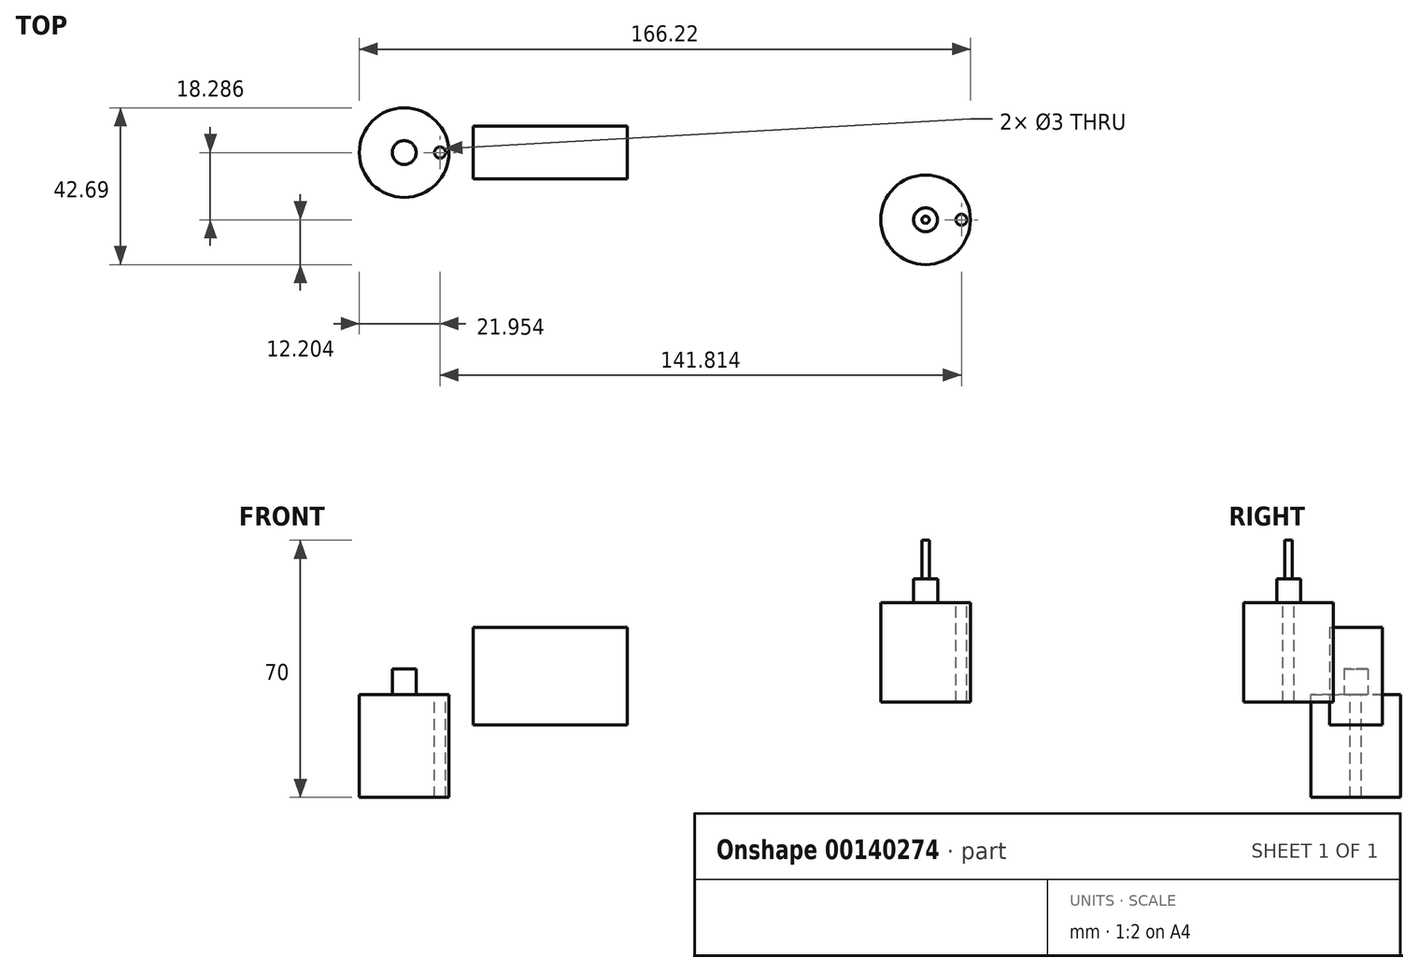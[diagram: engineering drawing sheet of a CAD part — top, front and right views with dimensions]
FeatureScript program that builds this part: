
annotation { "Feature Type Name" : "Feature", "Feature Type Description" : "" }
export const myFeature = defineFeature(function(context is Context, id is Id, definition is map)
    precondition{}
    {
        {
            var Q0;
            Q0=qCreatedBy(makeId("Front.planeOp"),FACE);
            var sketch = newSketch(context, id + "F0", { "sketchPlane" : qUnion([Q0])});
            skLineSegment(sketch, "E0.bottom", {"start": v(21, 13.25) * mm, "end": v(-21, 13.25) * mm});
            skLineSegment(sketch, "E0.top", {"start": v(21, -13.25) * mm, "end": v(-21, -13.25) * mm});
            skLineSegment(sketch, "E0.left", {"start": v(21, 13.25) * mm, "end": v(21, -13.25) * mm});
            skLineSegment(sketch, "E0.right", {"start": v(-21, 13.25) * mm, "end": v(-21, -13.25) * mm});
            skPoint(sketch, "E0.middle", {"position": v(0, 0) * mm});
            skSolve(sketch);
        }
        {
            var Q0;
            Q0 = qSketchRegion(id + "F0", true);
            extrude(context, id + "F1", {"entities" : qUnion([Q0]), "endBound" : BoundingType.SYMMETRIC, "depth" : 14.3 * mm});
        }
        {
            var Q0;
            Q0=makeQuery(id+"F1.opExtrude","CAP_FACE",FACE,{"disambiguationData":[OSD([sQuery(id+"F0.wireOp",EDGE,"E0.bottom"),sQuery(id+"F0.wireOp",EDGE,"E0.top"),sQuery(id+"F0.wireOp",EDGE,"E0.left"),sQuery(id+"F0.wireOp",EDGE,"E0.right")])],"isStart":false});
            cPlane(context, id + "F2", {"entities" : qUnion([Q0]), "cplaneType" : CPlaneType.OFFSET, "offset" : 0 * mm, "width" : 150 * mm, "height" : 150 * mm});
        }
        {
            var Q0;
            Q0=qCreatedBy(makeId("Top.planeOp"),FACE);
            var sketch = newSketch(context, id + "F3", { "sketchPlane" : qUnion([Q0])});
            skLineSegment(sketch, "E1", {"start": v(-39.74, 30.29) * mm, "end": v(-39.74, -34.47) * mm, "construction": true});
            skCircle(sketch, "E2", {"center": v(-39.74, 0) * mm, "radius": 12.2 * mm});
            skLineSegment(sketch, "E3.0", {"start": v(-49.49, 30.29) * mm, "end": v(-49.49, -34.47) * mm, "construction": true});
            skCircle(sketch, "E4", {"center": v(-49.49, 0) * mm, "radius": 1.5 * mm});
            skCircle(sketch, "E5.MirrorC", {"center": v(-29.99, 0) * mm, "radius": 1.5 * mm});
            skLineSegment(sketch, "E6.MirrorCS", {"start": v(-29.99, 30.29) * mm, "end": v(-29.99, -34.47) * mm, "construction": true});
            skCircle(sketch, "E7", {"center": v(-39.74, 0) * mm, "radius": 3.25 * mm});
            skCircle(sketch, "E8", {"center": v(-39.74, 0) * mm, "radius": 1 * mm});
            skSolve(sketch);
        }
        {
            var Q0;
            Q0=makeQuery(id+"F3.imprint","IMPRINT",FACE,{"disambiguationData":[TD([[makeQuery(id+"F3.imprint","IMPRINT",EDGE,{"derivedFrom":sQuery(id+"F3.wireOp",EDGE,"E4")}),1.0]])]});
            var Q1;
            Q1=makeQuery(id+"F3.imprint","IMPRINT",FACE,{"disambiguationData":[TD([[makeQuery(id+"F3.imprint","IMPRINT",EDGE,{"derivedFrom":sQuery(id+"F3.wireOp",EDGE,"E5.MirrorC")}),-1.0]])]});
            var Q2;
            Q2=makeQuery(id+"F3.imprint","IMPRINT",FACE,{"disambiguationData":[TD([[makeQuery(id+"F3.imprint","IMPRINT",EDGE,{"derivedFrom":sQuery(id+"F3.wireOp",EDGE,"E2")}),1.0]])]});
            var Q3;
            Q3=makeQuery(id+"F3.imprint","IMPRINT",FACE,{"disambiguationData":[TD([[makeQuery(id+"F3.imprint","IMPRINT",EDGE,{"derivedFrom":sQuery(id+"F3.wireOp",EDGE,"E7")}),1.0]])]});
            var Q4;
            Q4=makeQuery(id+"F3.imprint","IMPRINT",FACE,{"disambiguationData":[TD([[makeQuery(id+"F3.imprint","IMPRINT",EDGE,{"derivedFrom":sQuery(id+"F3.wireOp",EDGE,"E8")}),1.0]])]});
            extrude(context, id + "F4", {"entities" : qUnion([Q0, Q1, Q2, Q3, Q4]), "oppositeDirection" : true, "depth" : 33 * mm});
        }
        {
            var Q0;
            Q0=makeQuery(id+"F3.imprint","IMPRINT",FACE,{"disambiguationData":[TD([[makeQuery(id+"F3.imprint","IMPRINT",EDGE,{"derivedFrom":sQuery(id+"F3.wireOp",EDGE,"E8")}),1.0]])]});
            var Q1;
            Q1=makeQuery(id+"F3.imprint","IMPRINT",FACE,{"disambiguationData":[TD([[makeQuery(id+"F3.imprint","IMPRINT",EDGE,{"derivedFrom":sQuery(id+"F3.wireOp",EDGE,"E7")}),1.0]])]});
            extrude(context, id + "F5", {"entities" : qUnion([Q0, Q1]), "operationType" : NewBodyOperationType.ADD, "depth" : 2 * mm});
        }
        {
            var Q0;
            Q0=sQuery(id+"F3.wireOp",EDGE,"E8");
            extrude(context, id + "F6", {"bodyType" : ToolBodyType.SURFACE, "surfaceEntities" : qUnion([Q0]), "depth" : 12 * mm});
        }
        {
            var Q0;
            Q0=makeQuery(id+"F3.imprint","IMPRINT",FACE,{"disambiguationData":[TD([[makeQuery(id+"F3.imprint","IMPRINT",EDGE,{"derivedFrom":sQuery(id+"F3.wireOp",EDGE,"E4")}),1.0]])]});
            var Q1;
            Q1=makeQuery(id+"F3.imprint","IMPRINT",FACE,{"disambiguationData":[TD([[makeQuery(id+"F3.imprint","IMPRINT",EDGE,{"derivedFrom":sQuery(id+"F3.wireOp",EDGE,"E5.MirrorC")}),-1.0]])]});
            extrude(context, id + "F7", {"entities" : qUnion([Q0, Q1]), "operationType" : NewBodyOperationType.REMOVE, "oppositeDirection" : true, "depth" : 5 * mm});
        }
        {
            var Q0;
            Q0=qCreatedBy(makeId("Top.planeOp"),FACE);
            cPlane(context, id + "F8", {"entities" : qUnion([Q0]), "cplaneType" : CPlaneType.OFFSET, "offset" : 25 * mm, "width" : 150 * mm, "height" : 150 * mm});
        }
        {
            var Q0;
            Q0=qCreatedBy(id+"F8.planeOp",FACE);
            var sketch = newSketch(context, id + "F9", { "sketchPlane" : qUnion([Q0])});
            skLineSegment(sketch, "E9", {"start": v(102.08, 12) * mm, "end": v(102.08, -52.76) * mm, "construction": true});
            skCircle(sketch, "E10", {"center": v(102.08, -18.29) * mm, "radius": 12.2 * mm});
            skLineSegment(sketch, "E11.0", {"start": v(92.33, -3.52) * mm, "end": v(92.33, -33.05) * mm, "construction": true});
            skCircle(sketch, "E12", {"center": v(92.33, -18.29) * mm, "radius": 1.5 * mm});
            skCircle(sketch, "E13.MirrorC", {"center": v(111.83, -18.29) * mm, "radius": 1.5 * mm});
            skLineSegment(sketch, "E14.MirrorCS", {"start": v(111.83, -3.52) * mm, "end": v(111.83, -33.05) * mm, "construction": true});
            skCircle(sketch, "E15", {"center": v(102.08, -18.29) * mm, "radius": 3.25 * mm});
            skCircle(sketch, "E16", {"center": v(102.08, -18.29) * mm, "radius": 1 * mm});
            skLineSegment(sketch, "E17", {"start": v(148.87, -18.29) * mm, "end": v(55.3, -18.29) * mm});
            skSolve(sketch);
        }
        {
            var Q0;
            Q0=makeQuery(id+"F9.imprint","IMPRINT",FACE,{"disambiguationData":[TD([[makeQuery(id+"F9.imprint","IMPRINT",EDGE,{"derivedFrom":sQuery(id+"F9.wireOp",EDGE,"E10")}),1.0]])]});
            var Q1;
            Q1=makeQuery(id+"F9.imprint","IMPRINT",FACE,{"disambiguationData":[TD([[makeQuery(id+"F9.imprint","IMPRINT",EDGE,{"derivedFrom":sQuery(id+"F9.wireOp",EDGE,"E13.MirrorC")}),-1.0]])]});
            var Q2;
            Q2=makeQuery(id+"F9.imprint","IMPRINT",FACE,{"disambiguationData":[TD([[makeQuery(id+"F9.imprint","IMPRINT",EDGE,{"derivedFrom":sQuery(id+"F9.wireOp",EDGE,"E15")}),1.0]])]});
            var Q3;
            Q3=makeQuery(id+"F9.imprint","IMPRINT",FACE,{"disambiguationData":[TD([[makeQuery(id+"F9.imprint","IMPRINT",EDGE,{"derivedFrom":sQuery(id+"F9.wireOp",EDGE,"E16")}),1.0]])]});
            var Q4;
            Q4=makeQuery(id+"F9.imprint","IMPRINT",FACE,{"disambiguationData":[TD([[makeQuery(id+"F9.imprint","IMPRINT",EDGE,{"derivedFrom":sQuery(id+"F9.wireOp",EDGE,"E12")}),1.0]])]});
            extrude(context, id + "F10", {"entities" : qUnion([Q0, Q1, Q2, Q3, Q4]), "oppositeDirection" : true, "depth" : 32 * mm});
        }
        {
            var Q0;
            Q0=makeQuery(id+"F9.imprint","IMPRINT",FACE,{"disambiguationData":[TD([[makeQuery(id+"F9.imprint","IMPRINT",EDGE,{"derivedFrom":sQuery(id+"F9.wireOp",EDGE,"E12")}),1.0]])]});
            var Q1;
            Q1=makeQuery(id+"F9.imprint","IMPRINT",FACE,{"disambiguationData":[TD([[makeQuery(id+"F9.imprint","IMPRINT",EDGE,{"derivedFrom":sQuery(id+"F9.wireOp",EDGE,"E13.MirrorC")}),-1.0]])]});
            extrude(context, id + "F11", {"entities" : qUnion([Q0, Q1]), "operationType" : NewBodyOperationType.REMOVE, "oppositeDirection" : true, "depth" : 5 * mm});
        }
        {
            var Q0;
            Q0=makeQuery(id+"F9.imprint","IMPRINT",FACE,{"disambiguationData":[TD([[makeQuery(id+"F9.imprint","IMPRINT",EDGE,{"derivedFrom":sQuery(id+"F9.wireOp",EDGE,"E15")}),1.0]])]});
            extrude(context, id + "F12", {"entities" : qUnion([Q0]), "operationType" : NewBodyOperationType.ADD, "depth" : 1.5 * mm});
        }
        {
            var Q0;
            Q0=makeQuery(id+"F9.imprint","IMPRINT",FACE,{"disambiguationData":[TD([[makeQuery(id+"F9.imprint","IMPRINT",EDGE,{"derivedFrom":sQuery(id+"F9.wireOp",EDGE,"E16")}),1.0]])]});
            extrude(context, id + "F13", {"entities" : qUnion([Q0]), "operationType" : NewBodyOperationType.ADD, "depth" : 12 * mm});
        }
    });
